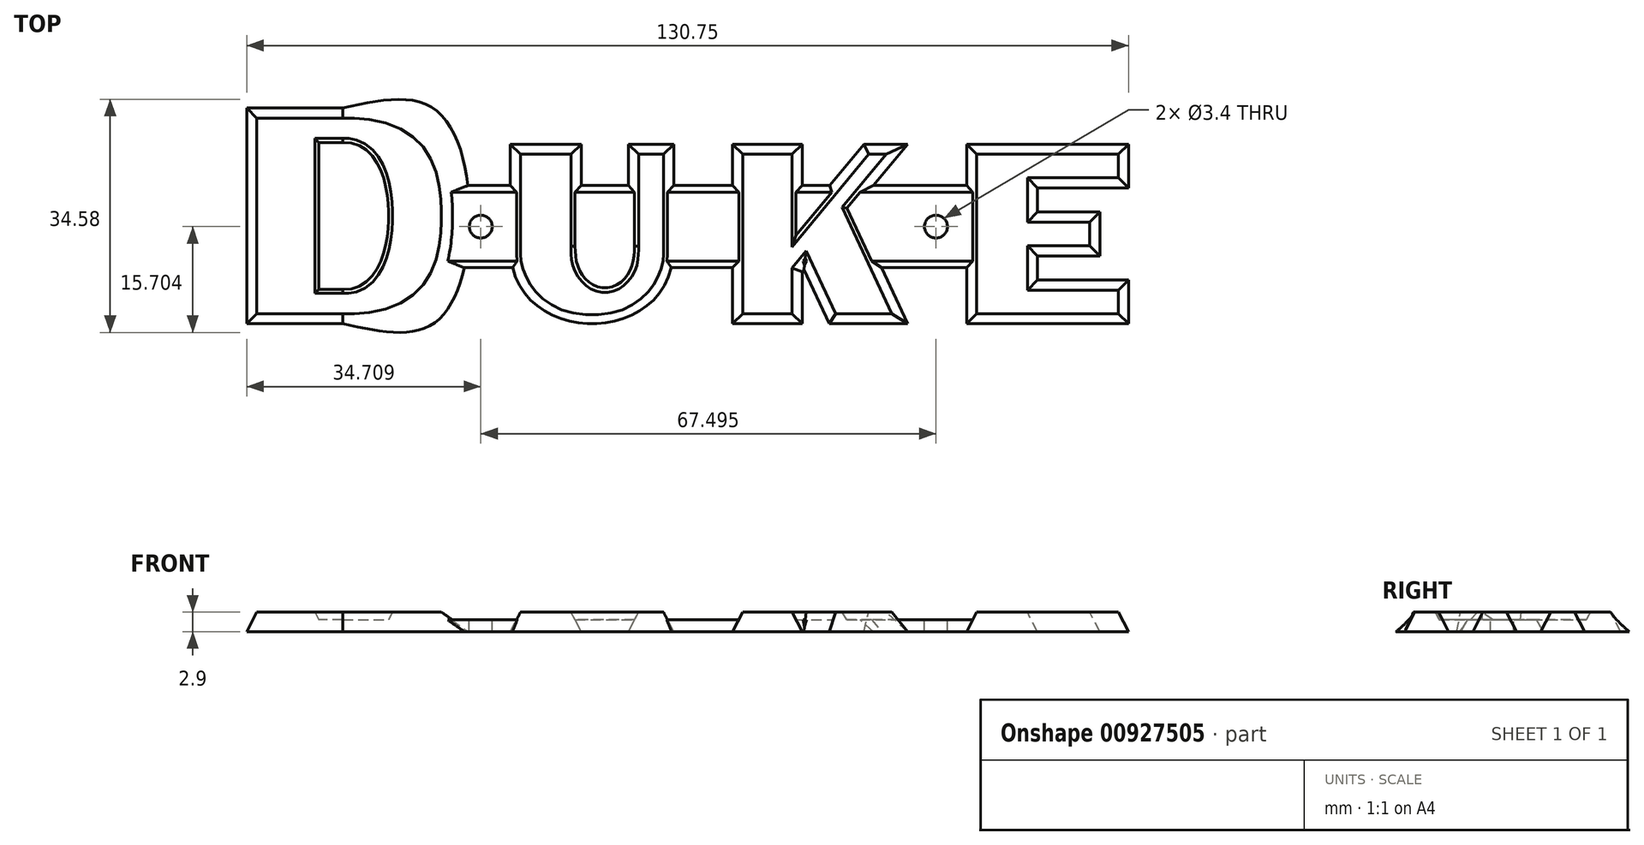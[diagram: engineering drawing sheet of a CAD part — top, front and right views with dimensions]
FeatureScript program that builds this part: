
annotation { "Feature Type Name" : "Feature", "Feature Type Description" : "" }
export const myFeature = defineFeature(function(context is Context, id is Id, definition is map)
    precondition{}
    {
        {
            var Q0;
            Q0=qCreatedBy(makeId("Top.planeOp"),FACE);
            var sketch = newSketch(context, id + "F0", { "sketchPlane" : qUnion([Q0])});
            skLineSegment(sketch, "E0", {"start": v(-71.03, -16) * mm, "end": v(-71.03, 16) * mm});
            skLineSegment(sketch, "E1", {"start": v(-59.43, -10) * mm, "end": v(-59.43, 10) * mm});
            skLineSegment(sketch, "E2", {"start": v(-59.43, 10) * mm, "end": v(-56.78, 10) * mm});
            skLineSegment(sketch, "E3", {"start": v(-56.78, -10) * mm, "end": v(-59.43, -10) * mm});
            skLineSegment(sketch, "E4", {"start": v(-7.73, 10.65) * mm, "end": v(-14.43, 10.65) * mm});
            skLineSegment(sketch, "E5", {"start": v(-21.43, 10.65) * mm, "end": v(-31.93, 10.65) * mm});
            skLineSegment(sketch, "E6", {"start": v(1.02, 10.65) * mm, "end": v(1.02, -16) * mm});
            skLineSegment(sketch, "E7", {"start": v(1.02, -16) * mm, "end": v(11.32, -16) * mm});
            skLineSegment(sketch, "E8", {"start": v(11.32, -16) * mm, "end": v(11.32, -8.28) * mm});
            skLineSegment(sketch, "E9", {"start": v(11.32, -8.28) * mm, "end": v(11.58, -7.97) * mm});
            skLineSegment(sketch, "E10", {"start": v(11.58, -7.97) * mm, "end": v(15.32, -16) * mm});
            skLineSegment(sketch, "E11", {"start": v(15.32, -16) * mm, "end": v(26.97, -16) * mm});
            skLineSegment(sketch, "E12", {"start": v(26.97, -16) * mm, "end": v(19.03, 1.04) * mm});
            skLineSegment(sketch, "E13", {"start": v(19.03, 1.04) * mm, "end": v(26.97, 10.65) * mm});
            skLineSegment(sketch, "E14", {"start": v(26.97, 10.65) * mm, "end": v(20.47, 10.65) * mm});
            skLineSegment(sketch, "E15", {"start": v(20.47, 10.65) * mm, "end": v(11.32, -0.42) * mm});
            skLineSegment(sketch, "E16", {"start": v(11.32, -0.42) * mm, "end": v(11.32, 10.65) * mm});
            skLineSegment(sketch, "E17", {"start": v(11.32, 10.65) * mm, "end": v(1.02, 10.65) * mm});
            skLineSegment(sketch, "E18", {"start": v(35.72, 10.65) * mm, "end": v(35.72, -16) * mm});
            skLineSegment(sketch, "E19", {"start": v(35.72, -16) * mm, "end": v(59.72, -16) * mm});
            skLineSegment(sketch, "E20", {"start": v(59.72, -16) * mm, "end": v(59.72, -9.5) * mm});
            skLineSegment(sketch, "E21", {"start": v(59.72, -9.5) * mm, "end": v(46.22, -9.5) * mm});
            skLineSegment(sketch, "E22", {"start": v(46.22, -9.5) * mm, "end": v(46.22, -5.93) * mm});
            skLineSegment(sketch, "E23", {"start": v(46.22, -5.93) * mm, "end": v(55.47, -5.93) * mm});
            skLineSegment(sketch, "E24", {"start": v(55.47, -5.92) * mm, "end": v(55.47, 0.58) * mm});
            skLineSegment(sketch, "E25", {"start": v(55.47, 0.57) * mm, "end": v(46.22, 0.57) * mm});
            skLineSegment(sketch, "E26", {"start": v(46.22, 0.58) * mm, "end": v(46.22, 4.15) * mm});
            skLineSegment(sketch, "E27", {"start": v(46.22, 4.15) * mm, "end": v(59.72, 4.15) * mm});
            skLineSegment(sketch, "E28", {"start": v(59.72, 4.15) * mm, "end": v(59.72, 10.65) * mm});
            skLineSegment(sketch, "E29", {"start": v(59.72, 10.65) * mm, "end": v(35.72, 10.65) * mm});
            skLineSegment(sketch, "E30", {"start": v(11.32, -16) * mm, "end": v(15.32, -16) * mm, "construction": true});
            skLineSegment(sketch, "E31", {"start": v(26.97, -16) * mm, "end": v(35.72, -16) * mm, "construction": true});
            skLineSegment(sketch, "E32", {"start": v(1.02, -16) * mm, "end": v(-19.83, -16) * mm, "construction": true});
            skLineSegment(sketch, "E33", {"start": v(11.32, -0.42) * mm, "end": v(11.32, -8.28) * mm, "construction": true});
            skLineSegment(sketch, "E34", {"start": v(11.58, -7.97) * mm, "end": v(19.03, 1.04) * mm, "construction": true});
            skLineSegment(sketch, "E35", {"start": v(-21.43, 10.65) * mm, "end": v(-21.43, -4.5) * mm});
            skLineSegment(sketch, "E36", {"start": v(-14.43, 10.65) * mm, "end": v(-14.43, -4.5) * mm});
            skFitSpline(sketch, "E37", {"points": [v(-21.43, -4.5) * mm, v(-14.43, -4.5) * mm], "startDerivative": vector(0, -20.7) * mm, "endDerivative": vector(0, 20.7) * mm});
            skLineSegment(sketch, "E38", {"start": v(-21.43, -11.4) * mm, "end": v(-14.43, -11.4) * mm, "construction": true});
            skLineSegment(sketch, "E39", {"start": v(-31.93, 10.65) * mm, "end": v(-31.93, -4.8) * mm});
            skLineSegment(sketch, "E40", {"start": v(-7.73, 10.65) * mm, "end": v(-7.73, -4.8) * mm});
            skFitSpline(sketch, "E41", {"points": [v(-31.93, -4.8) * mm, v(-7.73, -4.8) * mm], "startDerivative": vector(0, -44.8) * mm, "endDerivative": vector(0, 44.8) * mm});
            skLineSegment(sketch, "E42", {"start": v(-31.93, -19.73) * mm, "end": v(-7.73, -19.73) * mm, "construction": true});
            skLineSegment(sketch, "E43", {"start": v(-21.43, 10.65) * mm, "end": v(-14.43, 10.65) * mm});
            skLineSegment(sketch, "E44", {"start": v(-71.03, 16) * mm, "end": v(-56.78, 16) * mm});
            skLineSegment(sketch, "E45", {"start": v(-71.03, -16) * mm, "end": v(-56.78, -16) * mm});
            skLineSegment(sketch, "E46", {"start": v(-56.78, 16) * mm, "end": v(-56.78, -16) * mm, "construction": true});
            skFitSpline(sketch, "E47", {"points": [v(-56.78, 16) * mm, v(-40.68, 0) * mm, v(-56.78, -16) * mm], "startDerivative": vector(80.36, 0) * mm, "endDerivative": vector(-80.36, 0) * mm});
            skLineSegment(sketch, "E48", {"start": v(-56.78, -16) * mm, "end": v(-19.83, -16) * mm, "construction": true});
            skLineSegment(sketch, "E49", {"start": v(-71.03, 0) * mm, "end": v(-40.68, 0) * mm, "construction": true});
            skLineSegment(sketch, "E50", {"start": v(-43.39, 16) * mm, "end": v(-43.39, -16) * mm, "construction": true});
            skFitSpline(sketch, "E51", {"points": [v(-56.78, 10) * mm, v(-50.93, 0) * mm, v(-56.78, -10) * mm], "startDerivative": vector(26.22, 0) * mm, "endDerivative": vector(-26.22, 0) * mm});
            skLineSegment(sketch, "E52", {"start": v(-52.4, 10) * mm, "end": v(-52.4, -10) * mm, "construction": true});
            skPoint(sketch, "E53", {"position": v(-17.89, -15.87) * mm});
            skPoint(sketch, "E54", {"position": v(-17.89, -9.67) * mm});
            skLineSegment(sketch, "E55", {"start": v(-17.89, -15.87) * mm, "end": v(-17.89, -9.67) * mm, "construction": true});
            skLineSegment(sketch, "E56", {"start": v(11.32, 10.65) * mm, "end": v(20.47, 10.65) * mm, "construction": true});
            skLineSegment(sketch, "E57", {"start": v(26.97, 10.65) * mm, "end": v(26.97, -16) * mm, "construction": true});
            skLineSegment(sketch, "E58", {"start": v(26.97, 10.65) * mm, "end": v(35.72, 10.65) * mm, "construction": true});
            skLineSegment(sketch, "E59", {"start": v(1.02, 10.65) * mm, "end": v(-7.73, 10.65) * mm, "construction": true});
            skLineSegment(sketch, "E60", {"start": v(-40.68, 0) * mm, "end": v(-31.93, 0) * mm, "construction": true});
            skSolve(sketch);
        }
        {
            var Q0;
            Q0=qCreatedBy(makeId("Top.planeOp"),FACE);
            var sketch = newSketch(context, id + "F1", { "sketchPlane" : qUnion([Q0])});
            skLineSegment(sketch, "E61.0", {"start": v(-71.03, 16) * mm, "end": v(-56.78, 16) * mm});
            skLineSegment(sketch, "E62.0", {"start": v(-71.03, -16) * mm, "end": v(-71.03, 16) * mm});
            skFitSpline(sketch, "E63.0", {"points": [v(-56.78, 16) * mm, v(-43.39, 16) * mm, v(-37.97, 0) * mm, v(-43.39, -16) * mm, v(-56.78, -16) * mm]});
            skLineSegment(sketch, "E64.0", {"start": v(-71.03, -16) * mm, "end": v(-56.78, -16) * mm});
            skSolve(sketch);
        }
        {
            var Q0;
            Q0=qCreatedBy(makeId("Top.planeOp"),FACE);
            var sketch = newSketch(context, id + "F2", { "sketchPlane" : qUnion([Q0])});
            skLineSegment(sketch, "E65", {"start": v(42.73, 4.51) * mm, "end": v(-51.4, 4.51) * mm});
            skLineSegment(sketch, "E66", {"start": v(-52.67, -7.69) * mm, "end": v(42.73, -7.69) * mm});
            skLineSegment(sketch, "E67", {"start": v(42.73, 4.51) * mm, "end": v(42.73, -7.69) * mm});
            skFitSpline(sketch, "E68.0", {"points": [v(-56.78, 10) * mm, v(-52.4, 10) * mm, v(-49.44, 0) * mm, v(-52.4, -10) * mm, v(-56.78, -10) * mm]});
            skLineSegment(sketch, "E69", {"start": v(42.73, -1.59) * mm, "end": v(-50.98, -1.59) * mm, "construction": true});
            skLineSegment(sketch, "E70", {"start": v(54.78, -1.59) * mm, "end": v(42.73, -1.59) * mm, "construction": true});
            skSolve(sketch);
        }
        {
            var Q0;
            Q0=qCreatedBy(makeId("Top.planeOp"),FACE);
            cPlane(context, id + "F3", {"entities" : qUnion([Q0]), "cplaneType" : CPlaneType.OFFSET, "offset" : 1.75 * mm, "width" : 150 * mm, "height" : 150 * mm});
        }
        {
            var Q0;
            Q0=qCreatedBy(id+"F3.planeOp",FACE);
            var sketch = newSketch(context, id + "F4", { "sketchPlane" : qUnion([Q0])});
            skLineSegment(sketch, "E71.0", {"start": v(42.73, 4.51) * mm, "end": v(-51.4, 4.51) * mm, "construction": true});
            skLineSegment(sketch, "E72.0", {"start": v(-52.67, -7.69) * mm, "end": v(42.73, -7.69) * mm, "construction": true});
            skLineSegment(sketch, "E73.0", {"start": v(39.47, -7.69) * mm, "end": v(39.47, 4.51) * mm, "construction": true});
            skLineSegment(sketch, "E74", {"start": v(-51.2, 3.51) * mm, "end": v(39.47, 3.51) * mm});
            skLineSegment(sketch, "E75", {"start": v(39.47, 3.51) * mm, "end": v(39.47, -6.69) * mm});
            skLineSegment(sketch, "E76", {"start": v(39.47, -6.69) * mm, "end": v(-52.12, -6.69) * mm});
            skLineSegment(sketch, "E77", {"start": v(-4.34, 3.51) * mm, "end": v(-4.34, 4.51) * mm, "construction": true});
            skLineSegment(sketch, "E78", {"start": v(-4.34, -6.69) * mm, "end": v(-4.34, -7.69) * mm, "construction": true});
            skFitSpline(sketch, "E79.0", {"points": [v(-56.78, 10) * mm, v(-52.4, 10) * mm, v(-49.44, 0) * mm, v(-52.4, -10) * mm, v(-56.78, -10) * mm]});
            skSolve(sketch);
        }
        {
            var Q0;
            {var subQ0=sQuery(id+"F2.wireOp",EDGE,"E65");Q0=makeQuery(id+"F2.imprint","IMPRINT",FACE,{"disambiguationData":[TD([[makeQuery(id+"F2.imprint","IMPRINT",EDGE,{"derivedFrom":subQ0}),1.0]])]});}
            var Q1;
            {var subQ0=sQuery(id+"F4.wireOp",EDGE,"E74");Q1=makeQuery(id+"F4.imprint","IMPRINT",FACE,{"disambiguationData":[TD([[makeQuery(id+"F4.imprint","IMPRINT",EDGE,{"derivedFrom":subQ0}),-1.0]])]});}
            loft(context, id + "F5", {"sheetProfilesArray" : [{ "sheetProfileEntities" : qUnion([Q0]) }, { "sheetProfileEntities" : qUnion([Q1]) }]});
        }
        {
            var Q0;
            Q0=qCreatedBy(makeId("Top.planeOp"),FACE);
            cPlane(context, id + "F6", {"entities" : qUnion([Q0]), "cplaneType" : CPlaneType.OFFSET, "offset" : 2.9 * mm, "width" : 150 * mm, "height" : 150 * mm});
        }
        {
            var Q0;
            Q0=qCreatedBy(id+"F6.planeOp",FACE);
            var sketch = newSketch(context, id + "F7", { "sketchPlane" : qUnion([Q0])});
            skLineSegment(sketch, "E80.0", {"start": v(-69.53, 14.5) * mm, "end": v(-56.78, 14.5) * mm});
            skLineSegment(sketch, "E80.1", {"start": v(-69.53, -14.5) * mm, "end": v(-69.53, 14.5) * mm});
            skLineSegment(sketch, "E80.2", {"start": v(-69.53, -14.5) * mm, "end": v(-56.78, -14.5) * mm});
            skFitSpline(sketch, "E80.3", {"points": [v(-56.78, 14.5) * mm, v(-55.18, 14.5) * mm, v(-52.34, 14.26) * mm, v(-49.04, 13.31) * mm, v(-46.59, 11.9) * mm, v(-44.8, 10.13) * mm, v(-43.53, 8) * mm, v(-42.7, 5.56) * mm, v(-42.33, 3.3) * mm, v(-42.2, 1.43) * mm, v(-42.17, 0) * mm, v(-42.2, -1.43) * mm, v(-42.33, -3.3) * mm, v(-42.7, -5.56) * mm, v(-43.53, -8) * mm, v(-44.8, -10.13) * mm, v(-46.59, -11.9) * mm, v(-49.04, -13.31) * mm, v(-52.34, -14.26) * mm, v(-55.18, -14.5) * mm, v(-56.78, -14.5) * mm]});
            skLineSegment(sketch, "E81.0", {"start": v(-60.93, 11.5) * mm, "end": v(-56.78, 11.5) * mm});
            skLineSegment(sketch, "E81.1", {"start": v(-60.93, -11.5) * mm, "end": v(-60.93, 11.5) * mm});
            skLineSegment(sketch, "E81.2", {"start": v(-56.78, -11.5) * mm, "end": v(-60.93, -11.5) * mm});
            skFitSpline(sketch, "E81.3", {"points": [v(-56.78, 11.5) * mm, v(-56.1, 11.5) * mm, v(-54.77, 11.3) * mm, v(-53.08, 10.43) * mm, v(-51.77, 9.13) * mm, v(-50.82, 7.56) * mm, v(-50.15, 5.82) * mm, v(-49.72, 3.95) * mm, v(-49.47, 2) * mm, v(-49.4, 0) * mm, v(-49.47, -2) * mm, v(-49.72, -3.95) * mm, v(-50.15, -5.82) * mm, v(-50.82, -7.56) * mm, v(-51.77, -9.13) * mm, v(-53.08, -10.43) * mm, v(-54.77, -11.3) * mm, v(-56.1, -11.5) * mm, v(-56.78, -11.5) * mm]});
            skLineSegment(sketch, "E82.0", {"start": v(-22.93, 9.15) * mm, "end": v(-30.43, 9.15) * mm});
            skLineSegment(sketch, "E82.1", {"start": v(-22.93, 9.15) * mm, "end": v(-22.93, -4.5) * mm});
            skLineSegment(sketch, "E82.2", {"start": v(-30.43, 9.15) * mm, "end": v(-30.43, -4.8) * mm});
            skFitSpline(sketch, "E82.3", {"points": [v(-22.93, -4.5) * mm, v(-22.93, -5.49) * mm, v(-22.68, -7.28) * mm, v(-21.63, -9.4) * mm, v(-19.98, -10.83) * mm, v(-17.93, -11.34) * mm, v(-15.88, -10.83) * mm, v(-14.23, -9.4) * mm, v(-13.18, -7.28) * mm, v(-12.93, -5.49) * mm, v(-12.93, -4.5) * mm]});
            skFitSpline(sketch, "E82.4", {"points": [v(-30.43, -4.8) * mm, v(-30.43, -5.63) * mm, v(-30.26, -7.17) * mm, v(-29.59, -9.11) * mm, v(-28.57, -10.74) * mm, v(-26.8, -12.54) * mm, v(-23.9, -14.08) * mm, v(-19.83, -14.71) * mm, v(-15.75, -14.08) * mm, v(-12.86, -12.54) * mm, v(-11.08, -10.74) * mm, v(-10.06, -9.11) * mm, v(-9.4, -7.17) * mm, v(-9.23, -5.63) * mm, v(-9.23, -4.8) * mm]});
            skLineSegment(sketch, "E82.5", {"start": v(-9.23, 9.15) * mm, "end": v(-9.23, -4.8) * mm});
            skLineSegment(sketch, "E82.6", {"start": v(-9.23, 9.15) * mm, "end": v(-12.93, 9.15) * mm});
            skLineSegment(sketch, "E82.7", {"start": v(-12.93, 9.15) * mm, "end": v(-12.93, -4.5) * mm});
            skLineSegment(sketch, "E83.0", {"start": v(9.82, -14.5) * mm, "end": v(9.82, -7.74) * mm});
            skLineSegment(sketch, "E83.1", {"start": v(17.27, 1.26) * mm, "end": v(23.79, 9.15) * mm});
            skLineSegment(sketch, "E83.2", {"start": v(24.62, -14.5) * mm, "end": v(17.27, 1.26) * mm});
            skLineSegment(sketch, "E83.3", {"start": v(16.28, -14.5) * mm, "end": v(24.62, -14.5) * mm});
            skLineSegment(sketch, "E83.4", {"start": v(11.94, -5.19) * mm, "end": v(16.28, -14.5) * mm});
            skLineSegment(sketch, "E83.5", {"start": v(23.79, 9.15) * mm, "end": v(21.18, 9.15) * mm});
            skLineSegment(sketch, "E83.6", {"start": v(9.82, -7.74) * mm, "end": v(11.94, -5.19) * mm});
            skLineSegment(sketch, "E83.7", {"start": v(21.18, 9.15) * mm, "end": v(9.82, -4.59) * mm});
            skLineSegment(sketch, "E83.8", {"start": v(9.82, -4.59) * mm, "end": v(9.82, 9.15) * mm});
            skLineSegment(sketch, "E83.9", {"start": v(9.82, 9.15) * mm, "end": v(2.52, 9.15) * mm});
            skLineSegment(sketch, "E83.10", {"start": v(2.52, 9.15) * mm, "end": v(2.52, -14.5) * mm});
            skLineSegment(sketch, "E83.11", {"start": v(2.52, -14.5) * mm, "end": v(9.82, -14.5) * mm});
            skLineSegment(sketch, "E84.0", {"start": v(58.22, 9.15) * mm, "end": v(37.22, 9.15) * mm});
            skLineSegment(sketch, "E84.1", {"start": v(44.72, -11) * mm, "end": v(44.72, -4.43) * mm});
            skLineSegment(sketch, "E84.2", {"start": v(58.22, -11) * mm, "end": v(44.72, -11) * mm});
            skLineSegment(sketch, "E84.3", {"start": v(58.22, -14.5) * mm, "end": v(58.22, -11) * mm});
            skLineSegment(sketch, "E84.4", {"start": v(37.22, -14.5) * mm, "end": v(58.22, -14.5) * mm});
            skLineSegment(sketch, "E84.5", {"start": v(44.72, -4.43) * mm, "end": v(53.97, -4.43) * mm});
            skLineSegment(sketch, "E84.6", {"start": v(37.22, 9.15) * mm, "end": v(37.22, -14.5) * mm});
            skLineSegment(sketch, "E84.7", {"start": v(53.97, -4.43) * mm, "end": v(53.97, -0.93) * mm});
            skLineSegment(sketch, "E84.8", {"start": v(53.97, -0.93) * mm, "end": v(44.72, -0.93) * mm});
            skLineSegment(sketch, "E84.9", {"start": v(44.72, -0.93) * mm, "end": v(44.72, 5.65) * mm});
            skLineSegment(sketch, "E84.10", {"start": v(44.72, 5.65) * mm, "end": v(58.22, 5.65) * mm});
            skLineSegment(sketch, "E84.11", {"start": v(58.22, 5.65) * mm, "end": v(58.22, 9.15) * mm});
            skSolve(sketch);
        }
        {
            var Q0;
            Q0=qCreatedBy(id+"F6.planeOp",FACE);
            var sketch = newSketch(context, id + "F8", { "sketchPlane" : qUnion([Q0])});
            skLineSegment(sketch, "E85.0", {"start": v(-69.53, 14.5) * mm, "end": v(-56.78, 14.5) * mm});
            skLineSegment(sketch, "E86.0", {"start": v(-69.53, -14.5) * mm, "end": v(-69.53, 14.5) * mm});
            skLineSegment(sketch, "E87.0", {"start": v(-69.53, -14.5) * mm, "end": v(-56.78, -14.5) * mm});
            skFitSpline(sketch, "E88.0", {"points": [v(-56.78, 14.5) * mm, v(-55.18, 14.5) * mm, v(-52.34, 14.26) * mm, v(-49.04, 13.31) * mm, v(-46.59, 11.9) * mm, v(-44.8, 10.13) * mm, v(-43.53, 8) * mm, v(-42.7, 5.56) * mm, v(-42.33, 3.3) * mm, v(-42.2, 1.43) * mm, v(-42.17, 0) * mm, v(-42.2, -1.43) * mm, v(-42.33, -3.3) * mm, v(-42.7, -5.56) * mm, v(-43.53, -8) * mm, v(-44.8, -10.13) * mm, v(-46.59, -11.9) * mm, v(-49.04, -13.31) * mm, v(-52.34, -14.26) * mm, v(-55.18, -14.5) * mm, v(-56.78, -14.5) * mm]});
            skSolve(sketch);
        }
        {
            var Q1;
            Q1=makeQuery(id+"F1.imprint","IMPRINT",FACE,{"disambiguationData":[TD([[makeQuery(id+"F1.imprint","IMPRINT",EDGE,{"derivedFrom":sQuery(id+"F1.wireOp",EDGE,"E61.0")}),-1.0]])]});
            var Q2;
            Q2=makeQuery(id+"F8.imprint","IMPRINT",FACE,{"disambiguationData":[TD([[makeQuery(id+"F8.imprint","IMPRINT",EDGE,{"derivedFrom":sQuery(id+"F8.wireOp",EDGE,"E85.0")}),-1.0]])]});
            loft(context, id + "F9", {"operationType" : NewBodyOperationType.ADD, "sheetProfilesArray" : [{ "sheetProfileEntities" : qUnion([Q1]) }, { "sheetProfileEntities" : qUnion([Q2]) }]});
        }
        {
            var Q1;
            Q1=makeQuery(id+"F0.imprint","IMPRINT",FACE,{"disambiguationData":[TD([[makeQuery(id+"F0.imprint","IMPRINT",EDGE,{"derivedFrom":sQuery(id+"F0.wireOp",EDGE,"E4")}),1.0]])]});
            var Q2;
            Q2=makeQuery(id+"F7.imprint","IMPRINT",FACE,{"disambiguationData":[TD([[makeQuery(id+"F7.imprint","IMPRINT",EDGE,{"derivedFrom":sQuery(id+"F7.wireOp",EDGE,"E82.0")}),1.0]])]});
            loft(context, id + "F10", {"operationType" : NewBodyOperationType.ADD, "sheetProfilesArray" : [{ "sheetProfileEntities" : qUnion([Q1]) }, { "sheetProfileEntities" : qUnion([Q2]) }]});
        }
        {
            var Q1;
            Q1=makeQuery(id+"F0.imprint","IMPRINT",FACE,{"disambiguationData":[TD([[makeQuery(id+"F0.imprint","IMPRINT",EDGE,{"derivedFrom":sQuery(id+"F0.wireOp",EDGE,"E6")}),1.0]])]});
            var Q2;
            Q2=makeQuery(id+"F7.imprint","IMPRINT",FACE,{"disambiguationData":[TD([[makeQuery(id+"F7.imprint","IMPRINT",EDGE,{"derivedFrom":sQuery(id+"F7.wireOp",EDGE,"E83.0")}),1.0]])]});
            loft(context, id + "F11", {"operationType" : NewBodyOperationType.ADD, "sheetProfilesArray" : [{ "sheetProfileEntities" : qUnion([Q1]) }, { "sheetProfileEntities" : qUnion([Q2]) }]});
        }
        {
            var Q1;
            Q1=makeQuery(id+"F0.imprint","IMPRINT",FACE,{"disambiguationData":[TD([[makeQuery(id+"F0.imprint","IMPRINT",EDGE,{"derivedFrom":sQuery(id+"F0.wireOp",EDGE,"E18")}),1.0]])]});
            var Q2;
            Q2=makeQuery(id+"F7.imprint","IMPRINT",FACE,{"disambiguationData":[TD([[makeQuery(id+"F7.imprint","IMPRINT",EDGE,{"derivedFrom":sQuery(id+"F7.wireOp",EDGE,"E84.0")}),1.0]])]});
            loft(context, id + "F12", {"operationType" : NewBodyOperationType.ADD, "sheetProfilesArray" : [{ "sheetProfileEntities" : qUnion([Q1]) }, { "sheetProfileEntities" : qUnion([Q2]) }]});
        }
        {
            var Q1;
            Q1=makeQuery(id+"F7.imprint","IMPRINT",FACE,{"disambiguationData":[TD([[makeQuery(id+"F7.imprint","IMPRINT",EDGE,{"derivedFrom":sQuery(id+"F7.wireOp",EDGE,"E81.0")}),-1.0]])]});
            var Q2;
            Q2=makeQuery(id+"F0.imprint","IMPRINT",FACE,{"disambiguationData":[TD([[makeQuery(id+"F0.imprint","IMPRINT",EDGE,{"derivedFrom":sQuery(id+"F0.wireOp",EDGE,"E1")}),-1.0]])]});
            loft(context, id + "F13", {"operationType" : NewBodyOperationType.REMOVE, "sheetProfilesArray" : [{ "sheetProfileEntities" : qUnion([Q1]) }, { "sheetProfileEntities" : qUnion([Q2]) }]});
        }
        {
            var Q0;
            Q0=qCreatedBy(id+"F3.planeOp",FACE);
            var sketch = newSketch(context, id + "F14", { "sketchPlane" : qUnion([Q0])});
            skLineSegment(sketch, "E89.0", {"start": v(-60.93, -11.5) * mm, "end": v(-60.93, 11.5) * mm});
            skLineSegment(sketch, "E90.0", {"start": v(-60.93, 11.5) * mm, "end": v(-56.78, 11.5) * mm});
            skFitSpline(sketch, "E91.0", {"points": [v(-56.78, 11.5) * mm, v(-56.43, 11.5) * mm, v(-55.93, 11.46) * mm, v(-55.37, 11.36) * mm, v(-55.05, 11.28) * mm, v(-54.82, 11.2) * mm, v(-54.6, 11.13) * mm, v(-54.3, 11.02) * mm, v(-53.94, 10.85) * mm, v(-53.6, 10.66) * mm, v(-53.37, 10.51) * mm, v(-53.24, 10.42) * mm, v(-53.14, 10.35) * mm, v(-53.05, 10.29) * mm, v(-52.93, 10.2) * mm, v(-52.73, 10.03) * mm, v(-52.45, 9.78) * mm, v(-52.18, 9.5) * mm, v(-52, 9.3) * mm, v(-51.9, 9.18) * mm, v(-51.83, 9.08) * mm, v(-51.76, 9) * mm, v(-51.67, 8.88) * mm, v(-51.52, 8.67) * mm, v(-51.36, 8.42) * mm, v(-51.2, 8.16) * mm, v(-51.08, 7.96) * mm, v(-51, 7.78) * mm, v(-50.93, 7.66) * mm, v(-50.9, 7.59) * mm, v(-50.87, 7.53) * mm, v(-50.84, 7.49) * mm, v(-50.81, 7.42) * mm, v(-50.76, 7.3) * mm, v(-50.68, 7.14) * mm, v(-50.6, 6.94) * mm, v(-50.49, 6.66) * mm, v(-50.35, 6.3) * mm, v(-50.2, 5.87) * mm, v(-50.08, 5.4) * mm, v(-49.97, 5.01) * mm, v(-49.9, 4.69) * mm, v(-49.85, 4.44) * mm, v(-49.8, 4.23) * mm, v(-49.78, 4.08) * mm, v(-49.76, 4) * mm, v(-49.75, 3.93) * mm, v(-49.74, 3.88) * mm, v(-49.73, 3.8) * mm, v(-49.7, 3.67) * mm, v(-49.67, 3.47) * mm, v(-49.64, 3.24) * mm, v(-49.6, 2.92) * mm, v(-49.55, 2.53) * mm, v(-49.49, 1.88) * mm, v(-49.45, 1.2) * mm, v(-49.43, 0.52) * mm, v(-49.42, 0) * mm, v(-49.43, -0.52) * mm, v(-49.45, -1.2) * mm, v(-49.49, -1.88) * mm, v(-49.55, -2.53) * mm, v(-49.6, -2.92) * mm, v(-49.64, -3.24) * mm, v(-49.67, -3.47) * mm, v(-49.7, -3.67) * mm, v(-49.73, -3.8) * mm, v(-49.74, -3.88) * mm, v(-49.75, -3.93) * mm, v(-49.76, -4) * mm, v(-49.78, -4.08) * mm, v(-49.8, -4.23) * mm, v(-49.85, -4.44) * mm, v(-49.9, -4.69) * mm, v(-49.97, -5.01) * mm, v(-50.08, -5.4) * mm, v(-50.2, -5.87) * mm, v(-50.35, -6.3) * mm, v(-50.49, -6.66) * mm, v(-50.6, -6.94) * mm, v(-50.68, -7.14) * mm, v(-50.76, -7.3) * mm, v(-50.81, -7.42) * mm, v(-50.84, -7.49) * mm, v(-50.87, -7.53) * mm, v(-50.9, -7.59) * mm, v(-50.93, -7.66) * mm, v(-51, -7.78) * mm, v(-51.08, -7.96) * mm, v(-51.2, -8.16) * mm, v(-51.36, -8.42) * mm, v(-51.52, -8.67) * mm, v(-51.67, -8.88) * mm, v(-51.76, -9) * mm, v(-51.83, -9.08) * mm, v(-51.9, -9.18) * mm, v(-52, -9.3) * mm, v(-52.18, -9.5) * mm, v(-52.45, -9.78) * mm, v(-52.73, -10.03) * mm, v(-52.93, -10.2) * mm, v(-53.05, -10.29) * mm, v(-53.14, -10.35) * mm, v(-53.24, -10.42) * mm, v(-53.37, -10.51) * mm, v(-53.6, -10.66) * mm, v(-53.94, -10.85) * mm, v(-54.3, -11.02) * mm, v(-54.6, -11.13) * mm, v(-54.82, -11.2) * mm, v(-55.05, -11.28) * mm, v(-55.37, -11.36) * mm, v(-55.93, -11.46) * mm, v(-56.43, -11.5) * mm, v(-56.78, -11.5) * mm]});
            skLineSegment(sketch, "E92.0", {"start": v(-56.78, -11.5) * mm, "end": v(-60.93, -11.5) * mm});
            skLineSegment(sketch, "E93.0", {"start": v(-22.93, -4.5) * mm, "end": v(-22.93, 9.15) * mm});
            skFitSpline(sketch, "E94.0", {"points": [v(-12.93, -4.5) * mm, v(-12.93, -4.98) * mm, v(-12.97, -5.69) * mm, v(-13.1, -6.45) * mm, v(-13.2, -6.88) * mm, v(-13.32, -7.3) * mm, v(-13.48, -7.78) * mm, v(-13.72, -8.32) * mm, v(-14, -8.83) * mm, v(-14.43, -9.45) * mm, v(-14.92, -9.98) * mm, v(-15.5, -10.42) * mm, v(-15.94, -10.68) * mm, v(-16.41, -10.9) * mm, v(-16.9, -11.05) * mm, v(-17.42, -11.15) * mm, v(-17.93, -11.18) * mm, v(-18.44, -11.15) * mm, v(-19.11, -11.02) * mm, v(-19.76, -10.77) * mm, v(-20.36, -10.42) * mm, v(-20.93, -9.98) * mm, v(-21.42, -9.45) * mm, v(-21.85, -8.83) * mm, v(-22.13, -8.32) * mm, v(-22.37, -7.78) * mm, v(-22.54, -7.3) * mm, v(-22.65, -6.88) * mm, v(-22.75, -6.45) * mm, v(-22.88, -5.69) * mm, v(-22.93, -4.99) * mm, v(-22.93, -4.5) * mm]});
            skLineSegment(sketch, "E95.0", {"start": v(-12.93, 9.15) * mm, "end": v(-12.93, -4.5) * mm});
            skLineSegment(sketch, "E96.0", {"start": v(-13.52, 3.51) * mm, "end": v(-22.33, 3.51) * mm, "construction": true});
            skLineSegment(sketch, "E97", {"start": v(-22.93, 3.51) * mm, "end": v(-12.93, 3.51) * mm});
            skSolve(sketch);
        }
        {
            var Q0;
            Q0=makeQuery(id+"F14.imprint","IMPRINT",FACE,{"disambiguationData":[TD([[makeQuery(id+"F14.imprint","IMPRINT",EDGE,{"derivedFrom":sQuery(id+"F14.wireOp",EDGE,"E89.0")}),-1.0]])]});
            var Q1;
            {var subQ0=sQuery(id+"F14.wireOp",EDGE,"E94.0");Q1=makeQuery(id+"F14.imprint","IMPRINT",FACE,{"disambiguationData":[TD([[makeQuery(id+"F14.imprint","IMPRINT",EDGE,{"derivedFrom":subQ0}),-1.0]])]});}
            var Q2;
            {var subQ0=sQuery(id+"F2.wireOp",EDGE,"E65");Q2=makeQuery(id+"F12.boolean.opBoolean","MERGE",FACE,{"derivedFrom":[makeQuery(id+"F11.boolean.opBoolean","MERGE",FACE,{"derivedFrom":[makeQuery(id+"F9.boolean.opBoolean","MERGE",FACE,{"derivedFrom":[makeQuery(id+"F5.opLoft","CAP_FACE",FACE,{"disambiguationData":[OSD([makeQuery(id+"F2.imprint","IMPRINT",FACE,{"disambiguationData":[TD([[makeQuery(id+"F2.imprint","IMPRINT",EDGE,{"derivedFrom":subQ0}),1.0]])]})])],"isStart":true}),makeQuery(id+"F9.opLoft","CAP_FACE",FACE,{"disambiguationData":[OSD([makeQuery(id+"F1.imprint","IMPRINT",FACE,{"disambiguationData":[TD([[makeQuery(id+"F1.imprint","IMPRINT",EDGE,{"derivedFrom":sQuery(id+"F1.wireOp",EDGE,"E61.0")}),-1.0]])]})])],"isStart":true})]}),makeQuery(id+"F11.opLoft","CAP_FACE",FACE,{"disambiguationData":[OSD([makeQuery(id+"F0.imprint","IMPRINT",FACE,{"disambiguationData":[TD([[makeQuery(id+"F0.imprint","IMPRINT",EDGE,{"derivedFrom":sQuery(id+"F0.wireOp",EDGE,"E6")}),1.0]])]})])],"isStart":true})]}),makeQuery(id+"F12.opLoft","CAP_FACE",FACE,{"disambiguationData":[OSD([makeQuery(id+"F0.imprint","IMPRINT",FACE,{"disambiguationData":[TD([[makeQuery(id+"F0.imprint","IMPRINT",EDGE,{"derivedFrom":sQuery(id+"F0.wireOp",EDGE,"E18")}),1.0]])]})])],"isStart":true})]});}
            extrude(context, id + "F15", {"entities" : qUnion([Q0, Q1]), "operationType" : NewBodyOperationType.ADD, "endBound" : BoundingType.UP_TO_SURFACE, "oppositeDirection" : true, "depth" : 25 * mm, "endBoundEntityFace" : qUnion([Q2]), "offsetDistance" : 25 * mm});
        }
        {
            var Q0;
            {var subQ9=sQuery(id+"F4.wireOp",EDGE,"E74");Q0=makeQuery(id+"F10.boolean.opBoolean","SPLIT",FACE,{"disambiguationData":[TD([makeQuery(id+"F9.opLoft","SWEPT_FACE",FACE,{"disambiguationData":[OSD([sQuery(id+"F1.wireOp",EDGE,"E61.0"),sQuery(id+"F1.wireOp",EDGE,"E63.0"),sQuery(id+"F1.wireOp",EDGE,"E64.0"),sQuery(id+"F8.wireOp",EDGE,"E85.0"),sQuery(id+"F8.wireOp",EDGE,"E87.0"),sQuery(id+"F8.wireOp",EDGE,"E88.0")])]})])],"derivedFrom":makeQuery(id+"F5.opLoft","CAP_FACE",FACE,{"disambiguationData":[OSD([makeQuery(id+"F4.imprint","IMPRINT",FACE,{"disambiguationData":[TD([[makeQuery(id+"F4.imprint","IMPRINT",EDGE,{"derivedFrom":subQ9}),-1.0]])]})])],"isStart":true})});}
            var sketch = newSketch(context, id + "F16", { "sketchPlane" : qUnion([Q0])});
            skLineSegment(sketch, "E98", {"start": v(-36.32, 3.51) * mm, "end": v(-36.32, -1.59) * mm, "construction": true});
            skLineSegment(sketch, "E99", {"start": v(-36.32, -1.59) * mm, "end": v(-36.32, -6.69) * mm, "construction": true});
            skLineSegment(sketch, "E100", {"start": v(-41.62, -1.59) * mm, "end": v(-36.32, -1.59) * mm, "construction": true});
            skLineSegment(sketch, "E101", {"start": v(-31.02, -1.59) * mm, "end": v(-36.32, -1.59) * mm, "construction": true});
            skCircle(sketch, "E102", {"center": v(-36.32, -1.59) * mm, "radius": 1.7 * mm});
            skLineSegment(sketch, "E103", {"start": v(31.17, -6.69) * mm, "end": v(31.17, -1.59) * mm, "construction": true});
            skLineSegment(sketch, "E104", {"start": v(31.17, -1.59) * mm, "end": v(31.17, 3.51) * mm, "construction": true});
            skLineSegment(sketch, "E105", {"start": v(19.25, -1.59) * mm, "end": v(31.17, -1.59) * mm, "construction": true});
            skLineSegment(sketch, "E106", {"start": v(31.17, -1.59) * mm, "end": v(36.63, -1.59) * mm, "construction": true});
            skCircle(sketch, "E107", {"center": v(31.17, -1.59) * mm, "radius": 1.7 * mm});
            skPoint(sketch, "E108", {"position": v(32.87, -1.59) * mm});
            skSolve(sketch);
        }
        {
            var Q0;
            Q0=makeQuery(id+"F16.imprint","IMPRINT",FACE,{"disambiguationData":[TD([[makeQuery(id+"F16.imprint","IMPRINT",EDGE,{"derivedFrom":sQuery(id+"F16.wireOp",EDGE,"E102")}),1.0]])]});
            var Q1;
            Q1=makeQuery(id+"F16.imprint","IMPRINT",FACE,{"disambiguationData":[TD([[makeQuery(id+"F16.imprint","IMPRINT",EDGE,{"derivedFrom":sQuery(id+"F16.wireOp",EDGE,"E107")}),1.0]])]});
            extrude(context, id + "F17", {"entities" : qUnion([Q0, Q1]), "operationType" : NewBodyOperationType.REMOVE, "endBound" : BoundingType.THROUGH_ALL, "oppositeDirection" : true, "depth" : 25 * mm, "offsetDistance" : 25 * mm});
        }
    });
